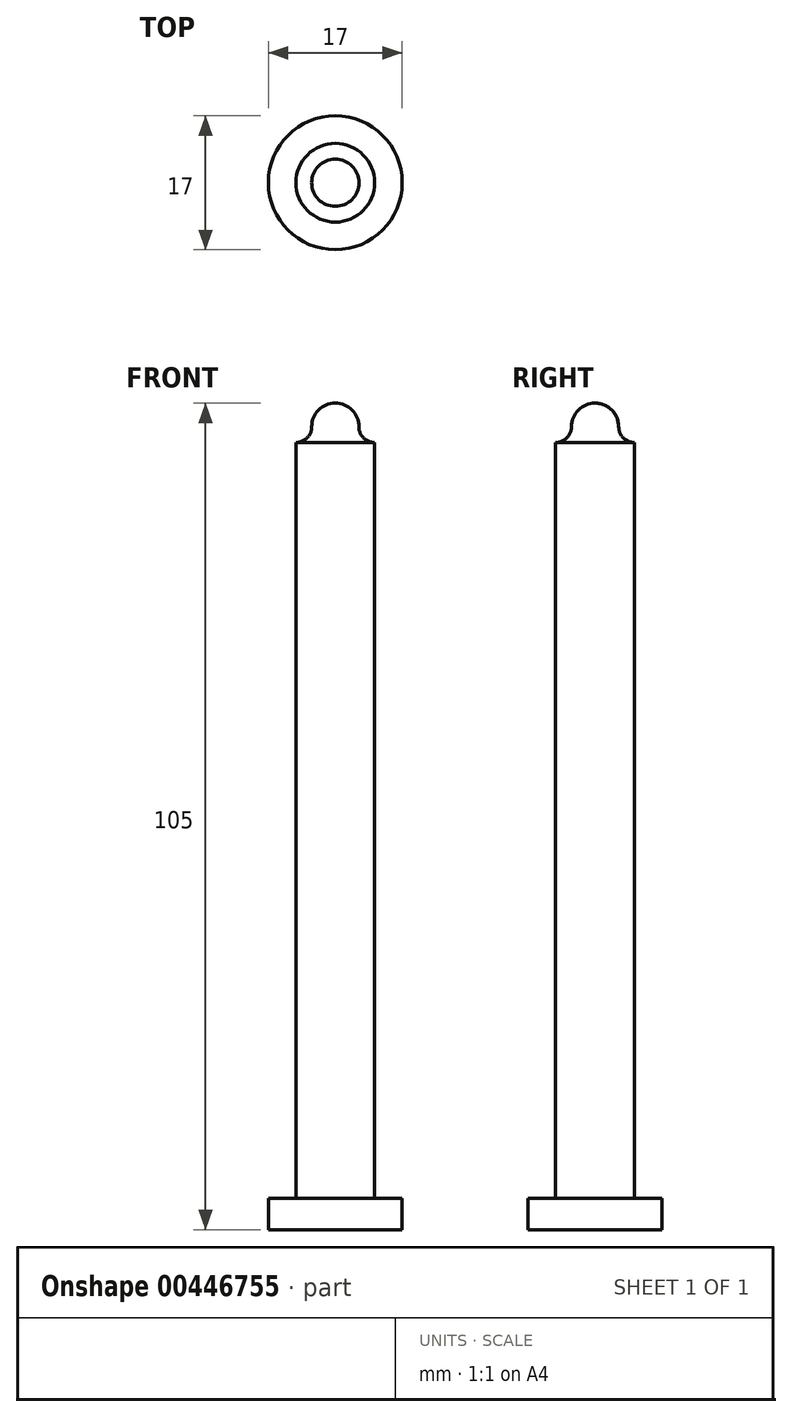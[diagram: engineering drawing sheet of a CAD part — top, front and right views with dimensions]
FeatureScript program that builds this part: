
annotation { "Feature Type Name" : "Feature", "Feature Type Description" : "" }
export const myFeature = defineFeature(function(context is Context, id is Id, definition is map)
    precondition{}
    {
        {
            var Q0;
            Q0=qCreatedBy(makeId("Top.planeOp"),FACE);
            var sketch = newSketch(context, id + "F0", { "sketchPlane" : qUnion([Q0])});
            skCircle(sketch, "E0", {"center": v(0, 0) * mm, "radius": 8.5 * mm});
            skSolve(sketch);
        }
        {
            var Q0;
            Q0=qSketchRegion(id+"F0",true);
            extrude(context, id + "F1", {"entities" : qUnion([Q0]), "depth" : 4 * mm});
        }
        {
            var Q0;
            Q0=qCreatedBy(makeId("Top.planeOp"),FACE);
            var sketch = newSketch(context, id + "F2", { "sketchPlane" : qUnion([Q0])});
            skCircle(sketch, "E1", {"center": v(0, 0) * mm, "radius": 5 * mm});
            skSolve(sketch);
        }
        {
            var Q0;
            Q0=qSketchRegion(id+"F2",true);
            extrude(context, id + "F3", {"entities" : qUnion([Q0]), "operationType" : NewBodyOperationType.ADD, "depth" : 100 * mm});
        }
        {
            var Q0;
            Q0=qCreatedBy(makeId("Right.planeOp"),FACE);
            var sketch = newSketch(context, id + "F4", { "sketchPlane" : qUnion([Q0])});
            skLineSegment(sketch, "E2", {"start": v(0, 102) * mm, "end": v(0, 100) * mm});
            skLineSegment(sketch, "E3", {"start": v(0, 100) * mm, "end": v(5, 100) * mm});
            skLineSegment(sketch, "E4", {"start": v(3, 102) * mm, "end": v(0, 102) * mm});
            skArc(sketch, "E5", {"start": v(3, 102) * mm, "mid": v(3.59, 100.59) * mm, "end": v(5, 100) * mm});
            skSolve(sketch);
        }
        {
            var Q0;
            Q0=makeQuery(id+"F4.imprint","IMPRINT",FACE,{"disambiguationData":[TD([[makeQuery(id+"F4.imprint","IMPRINT",EDGE,{"derivedFrom":sQuery(id+"F4.wireOp",EDGE,"E2")}),1.0]])]});
            var Q1;
            Q1=sQuery(id+"F4.wireOp",EDGE,"E2");
            revolve(context, id + "F5", {"operationType" : NewBodyOperationType.ADD, "entities" : qUnion([Q0]), "axis" : qUnion([Q1]), "revolveType" : RevolveType.FULL});
        }
        {
            var Q0;
            Q0=qCreatedBy(makeId("Right.planeOp"),FACE);
            var sketch = newSketch(context, id + "F6", { "sketchPlane" : qUnion([Q0])});
            skLineSegment(sketch, "E6", {"start": v(0, 102) * mm, "end": v(0, 105) * mm});
            skLineSegment(sketch, "E7", {"start": v(3, 102) * mm, "end": v(0, 102) * mm});
            skArc(sketch, "E8", {"start": v(3, 102) * mm, "mid": v(2.12, 104.12) * mm, "end": v(0, 105) * mm});
            skSolve(sketch);
        }
        {
            var Q0;
            Q0=makeQuery(id+"F6.imprint","IMPRINT",FACE,{"disambiguationData":[TD([[makeQuery(id+"F6.imprint","IMPRINT",EDGE,{"derivedFrom":sQuery(id+"F6.wireOp",EDGE,"E6")}),-1.0]])]});
            var Q1;
            Q1=sQuery(id+"F6.wireOp",EDGE,"E6");
            revolve(context, id + "F7", {"operationType" : NewBodyOperationType.ADD, "entities" : qUnion([Q0]), "axis" : qUnion([Q1]), "revolveType" : RevolveType.FULL});
        }
    });
